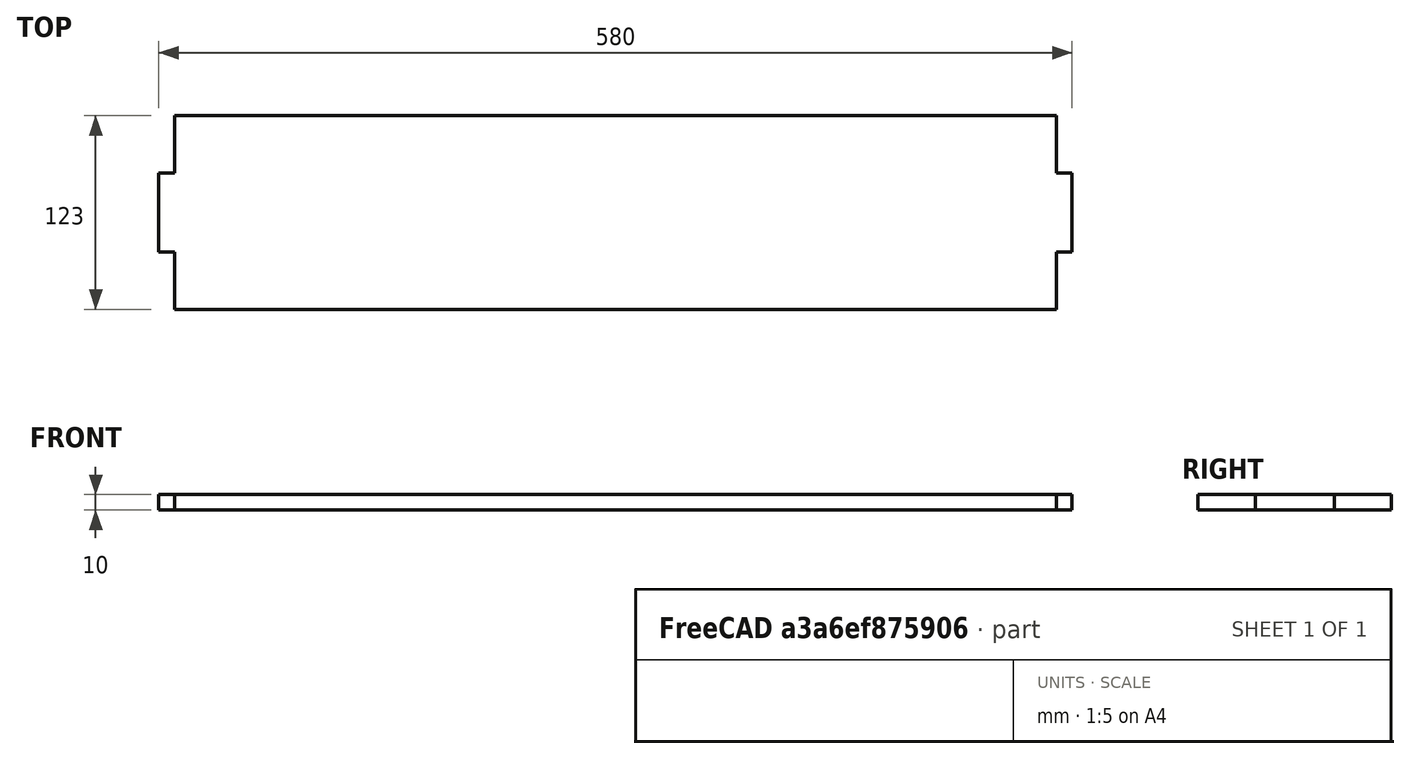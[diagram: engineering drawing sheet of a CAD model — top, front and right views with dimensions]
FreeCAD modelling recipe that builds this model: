
FCSTD DOCUMENT  (FreeCAD 0.16R)
Label: top
License: All rights reserved
LicenseURL: http://fr.wikipedia.org/wiki/<copyright redacted>
objects: Sketcher::SketchObject×1, PartDesign::Pad×1
note: 3 computed .brp shape members not serialized (recipe doc carries the construction recipe); baked Part::Feature solids carry a one-line shape summary decoded from their .brp

FEATURE [Sketcher::SketchObject] Sketch
  sketch-geometry (12):
    g0: LineSegment StartX=0 StartY=0 StartZ=0 EndX=560 EndY=0 EndZ=0
    g1: LineSegment StartX=560 StartY=123 StartZ=0 EndX=0 EndY=123 EndZ=0
    g2: LineSegment StartX=-10 StartY=86.5 StartZ=0 EndX=0 EndY=86.5 EndZ=0
    g3: LineSegment StartX=0 StartY=36.5 StartZ=0 EndX=-10 EndY=36.5 EndZ=0
    g4: LineSegment StartX=-10 StartY=36.5 StartZ=0 EndX=-10 EndY=86.5 EndZ=0
    g5: LineSegment StartX=560 StartY=86.5 StartZ=0 EndX=570 EndY=86.5 EndZ=0
    g6: LineSegment StartX=570 StartY=86.5 StartZ=0 EndX=570 EndY=36.5 EndZ=0
    g7: LineSegment StartX=570 StartY=36.5 StartZ=0 EndX=560 EndY=36.5 EndZ=0
    g8: LineSegment StartX=0 StartY=123 StartZ=0 EndX=0 EndY=86.5 EndZ=0
    g9: LineSegment StartX=0 StartY=0 StartZ=0 EndX=0 EndY=36.5 EndZ=0
    g10: LineSegment StartX=560 StartY=123 StartZ=0 EndX=560 EndY=86.5 EndZ=0
    g11: LineSegment StartX=560 StartY=36.5 StartZ=0 EndX=560 EndY=0 EndZ=0
  constraints (36):
    c: Horizontal(g0)
    c: Horizontal(g1)
    c: Coincident(g0,g-1)
    c: Distance(g0) = 560
    c: Coincident(g3,g4)
    c: Coincident(g4,g2)
    c: Horizontal(g2)
    c: Horizontal(g3)
    c: Vertical(g4)
    c: Coincident(g5,g6)
    c: Coincident(g6,g7)
    c: Horizontal(g5)
    c: Horizontal(g7)
    c: Vertical(g6)
    c: Equal(g5,g2)
    c: Equal(g4,g6)
    c: Distance(g5) = 10
    c: Distance(g6) = 50
    c: Equal(g3,g2)
    c: Equal(g2,g7)
    c: Coincident(g8,g1)
    c: Coincident(g8,g2)
    c: Vertical(g8)
    c: Coincident(g9,g-1)
    c: Coincident(g9,g3)
    c: Vertical(g9)
    c: DistanceY(g0,g1) = 123
    c: Coincident(g10,g1)
    c: Coincident(g10,g5)
    c: Coincident(g11,g7)
    c: Coincident(g11,g0)
    c: Vertical(g11)
    c: Vertical(g10)
    c: Equal(g10,g11)
    c: Equal(g11,g8)
    c: Equal(g8,g9)
FEATURE [PartDesign::Pad] Pad
  Length = 10
  Length2 = 100
  Sketch = -> Sketch
  Type = 0
